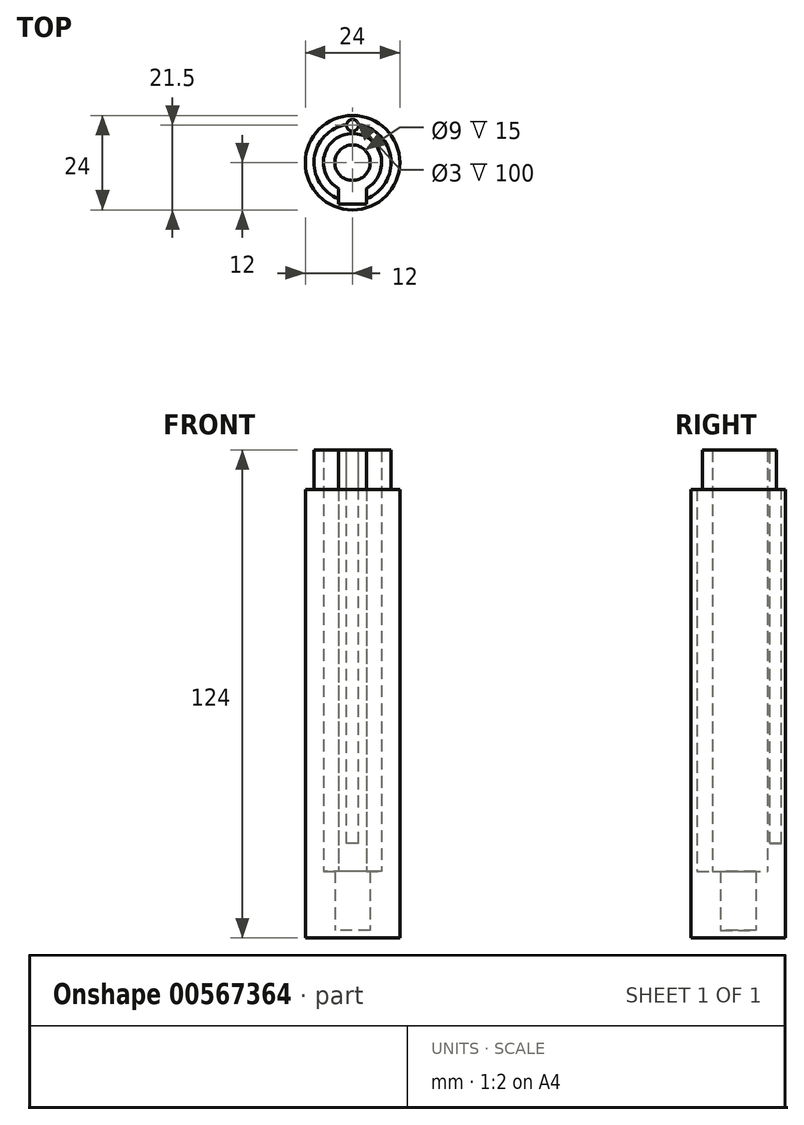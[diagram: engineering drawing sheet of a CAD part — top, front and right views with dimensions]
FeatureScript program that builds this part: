
annotation { "Feature Type Name" : "Feature", "Feature Type Description" : "" }
export const myFeature = defineFeature(function(context is Context, id is Id, definition is map)
    precondition{}
    {
        {
            var Q0;
            Q0=qCreatedBy(makeId("Top.planeOp"),FACE);
            var sketch = newSketch(context, id + "F0", { "sketchPlane" : qUnion([Q0])});
            skCircle(sketch, "E0", {"center": v(0, 0) * mm, "radius": 12 * mm});
            skSolve(sketch);
        }
        {
            var Q0;
            Q0=makeQuery(id+"F0.imprint","IMPRINT",FACE,{"disambiguationData":[TD([[makeQuery(id+"F0.imprint","IMPRINT",EDGE,{"derivedFrom":sQuery(id+"F0.wireOp",EDGE,"E0")}),1.0]])]});
            extrude(context, id + "F1", {"entities" : qUnion([Q0]), "depth" : 2 * mm, "offsetDistance" : 25 * mm});
        }
        {
            var Q0;
            Q0=makeQuery(id+"F1.opExtrude","CAP_FACE",FACE,{"disambiguationData":[OSD([sQuery(id+"F0.wireOp",EDGE,"E0")])],"isStart":false});
            var sketch = newSketch(context, id + "F2", { "sketchPlane" : qUnion([Q0])});
            skCircle(sketch, "E1", {"center": v(0, 0) * mm, "radius": 4.5 * mm});
            skCircle(sketch, "E2", {"center": v(0, 0) * mm, "radius": 12 * mm});
            skSolve(sketch);
        }
        {
            var Q0;
            Q0=makeQuery(id+"F2.imprint","IMPRINT",FACE,{"disambiguationData":[TD([[makeQuery(id+"F2.imprint","IMPRINT",EDGE,{"derivedFrom":sQuery(id+"F2.wireOp",EDGE,"E1")}),-1.0]])]});
            extrude(context, id + "F3", {"entities" : qUnion([Q0]), "operationType" : NewBodyOperationType.ADD, "depth" : 15 * mm, "offsetDistance" : 25 * mm});
        }
        {
            var Q0;
            Q0=makeQuery(id+"F3.opExtrude","CAP_FACE",FACE,{"disambiguationData":[OSD([sQuery(id+"F2.wireOp",EDGE,"E1"),sQuery(id+"F2.wireOp",EDGE,"E2")])],"isStart":false});
            var sketch = newSketch(context, id + "F4", { "sketchPlane" : qUnion([Q0])});
            skCircle(sketch, "E3", {"center": v(0, 0) * mm, "radius": 7.4 * mm});
            skCircle(sketch, "E4", {"center": v(0, 0) * mm, "radius": 12 * mm});
            skSolve(sketch);
        }
        {
            var Q0;
            Q0 = qSketchRegion(id + "F4", true);
            extrude(context, id + "F5", {"entities" : qUnion([Q0]), "operationType" : NewBodyOperationType.ADD, "depth" : 107 * mm, "offsetDistance" : 25 * mm});
        }
        {
            var Q0;
            Q0=makeQuery(id+"F3.opExtrude","CAP_FACE",FACE,{"disambiguationData":[OSD([sQuery(id+"F2.wireOp",EDGE,"E1"),sQuery(id+"F2.wireOp",EDGE,"E2")])],"isStart":false});
            var sketch = newSketch(context, id + "F6", { "sketchPlane" : qUnion([Q0])});
            skLineSegment(sketch, "E5", {"start": v(0, 0) * mm, "end": v(3.5, 0) * mm});
            skLineSegment(sketch, "E6", {"start": v(3.5, 0) * mm, "end": v(3.5, -10.5) * mm});
            skLineSegment(sketch, "E7", {"start": v(3.5, -10.5) * mm, "end": v(-3.5, -10.5) * mm});
            skLineSegment(sketch, "E8", {"start": v(-3.5, -10.5) * mm, "end": v(-3.5, 0) * mm});
            skLineSegment(sketch, "E9", {"start": v(-3.5, 0) * mm, "end": v(0, 0) * mm});
            skSolve(sketch);
        }
        {
            var Q0;
            Q0 = qSketchRegion(id + "F6", true);
            extrude(context, id + "F7", {"entities" : qUnion([Q0]), "operationType" : NewBodyOperationType.REMOVE, "endBound" : BoundingType.THROUGH_ALL, "depth" : 25 * mm, "offsetDistance" : 25 * mm});
        }
        {
            var Q0;
            Q0=makeQuery(id+"F5.opExtrude","CAP_FACE",FACE,{"disambiguationData":[OSD([sQuery(id+"F4.wireOp",EDGE,"E3"),sQuery(id+"F4.wireOp",EDGE,"E4")])],"isStart":false});
            var sketch = newSketch(context, id + "F8", { "sketchPlane" : qUnion([Q0])});
            skPoint(sketch, "E10.endSnap0", {"position": v(0, 7.4) * mm});
            skCircle(sketch, "E11", {"center": v(0, 9.5) * mm, "radius": 1.5 * mm});
            skSolve(sketch);
        }
        {
            var Q0;
            Q0=makeQuery(id+"F8.imprint","IMPRINT",FACE,{"disambiguationData":[TD([[makeQuery(id+"F8.imprint","IMPRINT",EDGE,{"derivedFrom":sQuery(id+"F8.wireOp",EDGE,"E11")}),1.0]])]});
            extrude(context, id + "F9", {"entities" : qUnion([Q0]), "operationType" : NewBodyOperationType.REMOVE, "oppositeDirection" : true, "depth" : 100 * mm, "offsetDistance" : 25 * mm});
        }
        {
            var Q0;
            Q0=makeQuery(id+"F5.opExtrude","CAP_FACE",FACE,{"disambiguationData":[OSD([sQuery(id+"F4.wireOp",EDGE,"E3"),sQuery(id+"F4.wireOp",EDGE,"E4")])],"isStart":false});
            var sketch = newSketch(context, id + "F10", { "sketchPlane" : qUnion([Q0])});
            skCircle(sketch, "E12", {"center": v(0, 0) * mm, "radius": 9.8 * mm});
            skCircle(sketch, "E13", {"center": v(0, 0) * mm, "radius": 12 * mm});
            skSolve(sketch);
        }
        {
            var Q0;
            Q0=makeQuery(id+"F10.imprint","IMPRINT",FACE,{"disambiguationData":[TD([[makeQuery(id+"F10.imprint","IMPRINT",EDGE,{"derivedFrom":sQuery(id+"F10.wireOp",EDGE,"E13")}),1.0]])]});
            extrude(context, id + "F11", {"entities" : qUnion([Q0]), "operationType" : NewBodyOperationType.REMOVE, "oppositeDirection" : true, "depth" : 10 * mm, "offsetDistance" : 25 * mm});
        }
        {
            var Q0;
            {var subQ2=sQuery(id+"F4.wireOp",EDGE,"E3");var subQ4=makeQuery(id+"F5.opExtrude","CAP_FACE",FACE,{"disambiguationData":[OSD([subQ2,sQuery(id+"F4.wireOp",EDGE,"E4")])],"isStart":false});Q0=makeQuery(id+"F11.boolean.opBoolean","SPLIT",FACE,{"disambiguationData":[TD([makeQuery(id+"F5.opExtrude","SWEPT_FACE",FACE,{"disambiguationData":[OSD([subQ2])]})])],"derivedFrom":subQ4});}
            var sketch = newSketch(context, id + "F12", { "sketchPlane" : qUnion([Q0])});
            skLineSegment(sketch, "E14", {"start": v(0, 0) * mm, "end": v(3.5, 0) * mm});
            skLineSegment(sketch, "E15", {"start": v(3.5, 0) * mm, "end": v(3.5, -12) * mm});
            skLineSegment(sketch, "E16", {"start": v(3.5, -12) * mm, "end": v(-3.5, -12) * mm});
            skLineSegment(sketch, "E17", {"start": v(-3.5, -12) * mm, "end": v(-3.5, 0) * mm});
            skLineSegment(sketch, "E18", {"start": v(-3.5, 0) * mm, "end": v(0, 0) * mm});
            skSolve(sketch);
        }
        {
            var Q0;
            Q0 = qSketchRegion(id + "F12", true);
            extrude(context, id + "F13", {"entities" : qUnion([Q0]), "operationType" : NewBodyOperationType.REMOVE, "oppositeDirection" : true, "depth" : 10 * mm, "offsetDistance" : 25 * mm});
        }
    });
